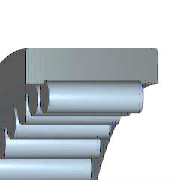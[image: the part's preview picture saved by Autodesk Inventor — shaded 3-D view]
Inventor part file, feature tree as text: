
AUTODESK INVENTOR PART (.ipt)
format: ipt  version: 2015 (Build 190159000, 159)  size: 203,776 bytes
history: native  units: mm (DEFAULTED — no unit token found)
features: sketch x1, other x1, pattern_circular x1
ambient origin geometry x8: Origin, YZ Plane, XZ Plane, XY Plane, X Axis, Y Axis, Z Axis, Center Point
bodies: Solid1 (feature_tree), Body (feature_tree)
feature tree (3):
  sketch  "Sketch"  dims[d6=90.0deg d0=0.15mm d8=90.0deg d1=70.0mm d2=360.0deg d3=0.0mm d4=0.0mm d5=0.0mm d7=8.0mm d9=15.0mm d11=13.0mm d12=12.5mm d13=1.428571mm d14=10.0mm]
  other  "Roller"
  pattern_circular  "Rollers"  [2 undecoded]
note: 2 required parameter values undecoded (feature->parameter linkage not recoverable at this tier; creation-order binding heuristic only, values carry confidence <= 0.55)
